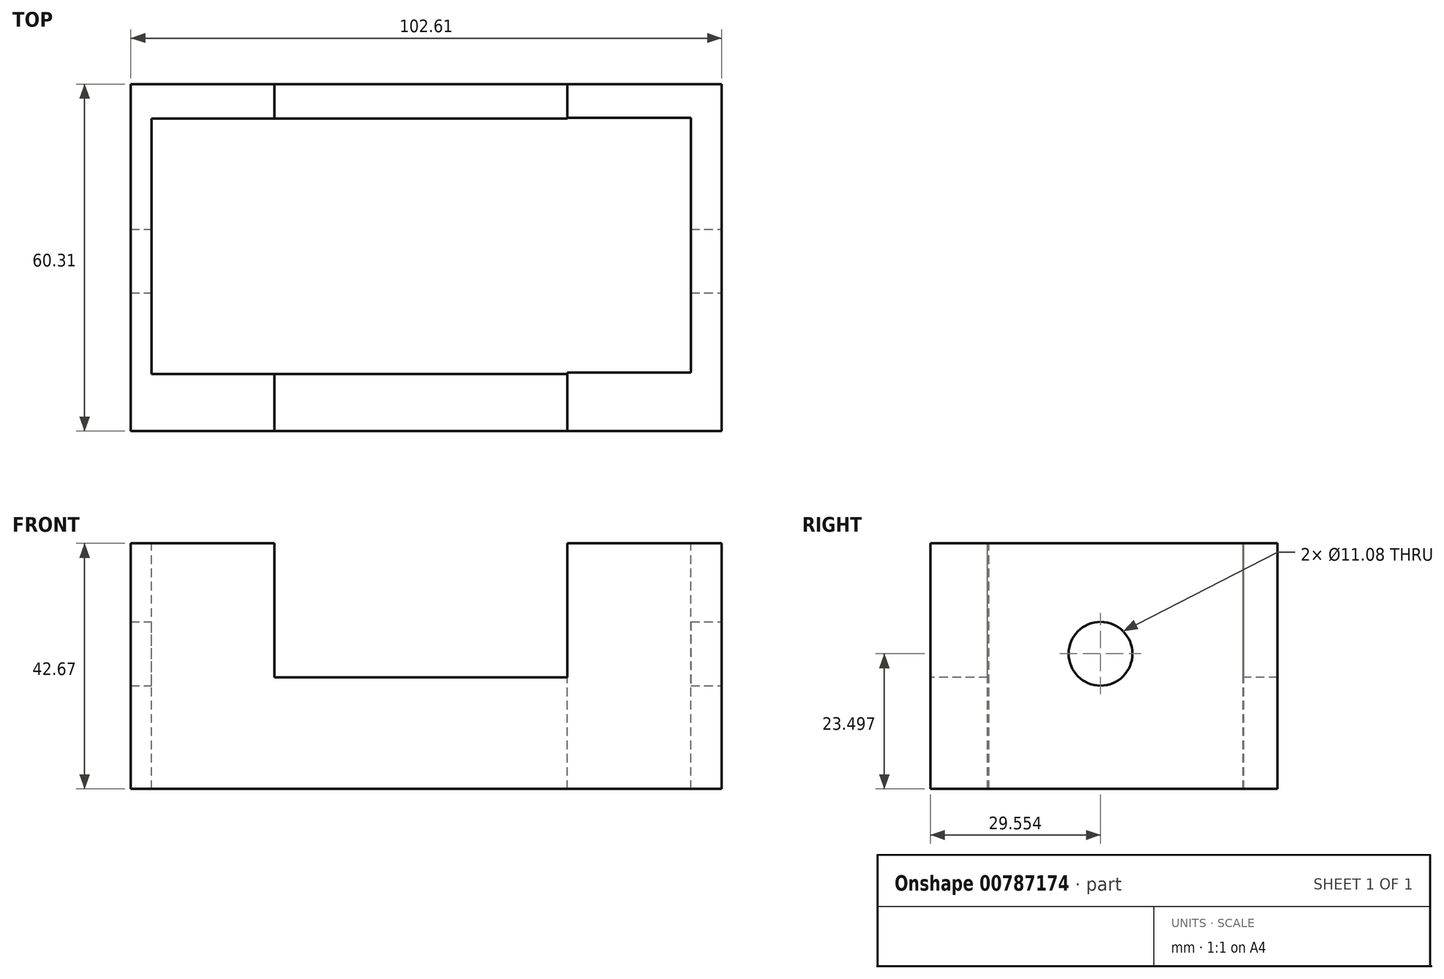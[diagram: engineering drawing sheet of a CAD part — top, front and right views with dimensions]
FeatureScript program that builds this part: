
annotation { "Feature Type Name" : "Feature", "Feature Type Description" : "" }
export const myFeature = defineFeature(function(context is Context, id is Id, definition is map)
    precondition{}
    {
        {
            var Q0;
            Q0=qCreatedBy(makeId("Top.planeOp"),FACE);
            var sketch = newSketch(context, id + "F0", { "sketchPlane" : qUnion([Q0])});
            skLineSegment(sketch, "E0.bottom", {"start": v(-54.23, 12.77) * mm, "end": v(48.38, 12.77) * mm});
            skLineSegment(sketch, "E0.top", {"start": v(-54.23, -47.54) * mm, "end": v(48.38, -47.54) * mm});
            skLineSegment(sketch, "E0.left", {"start": v(-54.23, 12.77) * mm, "end": v(-54.23, -47.54) * mm});
            skLineSegment(sketch, "E0.right", {"start": v(48.38, 12.77) * mm, "end": v(48.38, -47.54) * mm});
            skSolve(sketch);
        }
        {
            var Q0;
            Q0 = qSketchRegion(id + "F0", true);
            extrude(context, id + "F1", {"entities" : qUnion([Q0]), "depth" : 42.67 * mm, "offsetDistance" : 25.4 * mm});
        }
        {
            var Q0;
            Q0=makeQuery(id+"F1.opExtrude","SWEPT_FACE",FACE,{"disambiguationData":[OSD([sQuery(id+"F0.wireOp",EDGE,"E0.top")])]});
            var sketch = newSketch(context, id + "F2", { "sketchPlane" : qUnion([Q0])});
            skLineSegment(sketch, "E1", {"start": v(-29.28, 42.67) * mm, "end": v(-29.28, 19.4) * mm});
            skLineSegment(sketch, "E2", {"start": v(-29.28, 19.4) * mm, "end": v(21.57, 19.4) * mm});
            skLineSegment(sketch, "E3", {"start": v(21.57, 19.4) * mm, "end": v(21.57, 42.67) * mm});
            skLineSegment(sketch, "E4", {"start": v(21.57, 42.67) * mm, "end": v(-29.28, 42.67) * mm});
            skSolve(sketch);
        }
        {
            var Q0;
            Q0=makeQuery(id+"F2.imprint","IMPRINT",FACE,{"disambiguationData":[TD([[makeQuery(id+"F2.imprint","IMPRINT",EDGE,{"derivedFrom":sQuery(id+"F2.wireOp",EDGE,"E1")}),1.0]])]});
            extrude(context, id + "F3", {"entities" : qUnion([Q0]), "operationType" : NewBodyOperationType.REMOVE, "oppositeDirection" : true, "depth" : 108.7 * mm, "offsetDistance" : 25.4 * mm});
        }
        {
            var Q0;
            {var subQ0=sQuery(id+"F0.wireOp",EDGE,"E0.bottom");var subQ1=sQuery(id+"F0.wireOp",EDGE,"E0.top");var subQ2=sQuery(id+"F0.wireOp",EDGE,"E0.left");Q0=makeQuery(id+"F3.boolean.opBoolean","SPLIT",FACE,{"disambiguationData":[TD([makeQuery(id+"F1.opExtrude","SWEPT_FACE",FACE,{"disambiguationData":[OSD([subQ2])]})])],"derivedFrom":makeQuery(id+"F1.opExtrude","CAP_FACE",FACE,{"disambiguationData":[OSD([subQ0,subQ1,subQ2,sQuery(id+"F0.wireOp",EDGE,"E0.right")])],"isStart":false})});}
            var sketch = newSketch(context, id + "F4", { "sketchPlane" : qUnion([Q0])});
            skLineSegment(sketch, "E5", {"start": v(-54.23, -37.6) * mm, "end": v(-29.28, -37.6) * mm});
            skLineSegment(sketch, "E6", {"start": v(-50.59, -37.6) * mm, "end": v(-50.59, 6.75) * mm});
            skLineSegment(sketch, "E7", {"start": v(-29.28, 6.75) * mm, "end": v(-50.59, 6.75) * mm});
            skSolve(sketch);
        }
        {
            var Q0;
            {var subQ3=sQuery(id+"F4.wireOp",EDGE,"E6");Q0=makeQuery(id+"F4.imprint","IMPRINT",FACE,{"disambiguationData":[TD([[makeQuery(id+"F4.imprint","IMPRINT",EDGE,{"derivedFrom":subQ3}),-1.0]])]});}
            extrude(context, id + "F5", {"entities" : qUnion([Q0]), "operationType" : NewBodyOperationType.REMOVE, "oppositeDirection" : true, "depth" : 70.61 * mm, "offsetDistance" : 25.4 * mm});
        }
        {
            var Q0;
            Q0=makeQuery(id+"F3.boolean.opBoolean","COPY",FACE,{"derivedFrom":makeQuery(id+"F3.opExtrude","SWEPT_FACE",FACE,{"disambiguationData":[OSD([sQuery(id+"F2.wireOp",EDGE,"E2")])]})});
            var sketch = newSketch(context, id + "F6", { "sketchPlane" : qUnion([Q0])});
            skLineSegment(sketch, "E8", {"start": v(-29.28, -37.6) * mm, "end": v(21.57, -37.6) * mm});
            skLineSegment(sketch, "E9", {"start": v(-29.28, 6.75) * mm, "end": v(21.57, 6.75) * mm});
            skSolve(sketch);
        }
        {
            var Q0;
            {var subQ0=sQuery(id+"F6.wireOp",EDGE,"E8");Q0=makeQuery(id+"F6.imprint","IMPRINT",FACE,{"disambiguationData":[TD([[makeQuery(id+"F6.imprint","IMPRINT",EDGE,{"derivedFrom":subQ0}),1.0]])]});}
            extrude(context, id + "F7", {"entities" : qUnion([Q0]), "operationType" : NewBodyOperationType.REMOVE, "oppositeDirection" : true, "depth" : 37.6 * mm, "offsetDistance" : 25.4 * mm});
        }
        {
            var Q0;
            {var subQ0=sQuery(id+"F0.wireOp",EDGE,"E0.bottom");var subQ1=sQuery(id+"F0.wireOp",EDGE,"E0.right");var subQ2=sQuery(id+"F0.wireOp",EDGE,"E0.top");Q0=makeQuery(id+"F3.boolean.opBoolean","SPLIT",FACE,{"disambiguationData":[TD([makeQuery(id+"F1.opExtrude","SWEPT_FACE",FACE,{"disambiguationData":[OSD([subQ1])]})])],"derivedFrom":makeQuery(id+"F1.opExtrude","CAP_FACE",FACE,{"disambiguationData":[OSD([subQ0,subQ2,sQuery(id+"F0.wireOp",EDGE,"E0.left"),subQ1])],"isStart":false})});}
            var sketch = newSketch(context, id + "F8", { "sketchPlane" : qUnion([Q0])});
            skLineSegment(sketch, "E10", {"start": v(21.57, 6.92) * mm, "end": v(48.38, 6.92) * mm});
            skLineSegment(sketch, "E11", {"start": v(48.38, 6.92) * mm, "end": v(43.05, 6.92) * mm});
            skLineSegment(sketch, "E12", {"start": v(43.05, 6.92) * mm, "end": v(43.05, -37.39) * mm});
            skLineSegment(sketch, "E13", {"start": v(43.05, -37.39) * mm, "end": v(21.57, -37.39) * mm});
            skSolve(sketch);
        }
        {
            var Q0;
            {var subQ0=sQuery(id+"F8.wireOp",EDGE,"E10");Q0=makeQuery(id+"F8.imprint","IMPRINT",FACE,{"disambiguationData":[TD([[makeQuery(id+"F8.imprint","IMPRINT",EDGE,{"derivedFrom":subQ0}),-1.0]])]});}
            extrude(context, id + "F9", {"entities" : qUnion([Q0]), "operationType" : NewBodyOperationType.REMOVE, "oppositeDirection" : true, "depth" : 71.88 * mm, "offsetDistance" : 25.4 * mm});
        }
        {
            var Q0;
            Q0=makeQuery(id+"F1.opExtrude","SWEPT_FACE",FACE,{"disambiguationData":[OSD([sQuery(id+"F0.wireOp",EDGE,"E0.right")])]});
            var sketch = newSketch(context, id + "F10", { "sketchPlane" : qUnion([Q0])});
            skCircle(sketch, "E14", {"center": v(-17.99, 23.5) * mm, "radius": 5.54 * mm});
            skSolve(sketch);
        }
        {
            var Q0;
            Q0=makeQuery(id+"F10.imprint","IMPRINT",FACE,{"disambiguationData":[TD([[makeQuery(id+"F10.imprint","IMPRINT",EDGE,{"derivedFrom":sQuery(id+"F10.wireOp",EDGE,"E14")}),1.0]])]});
            extrude(context, id + "F11", {"entities" : qUnion([Q0]), "operationType" : NewBodyOperationType.REMOVE, "oppositeDirection" : true, "depth" : 182.63 * mm, "offsetDistance" : 25.4 * mm});
        }
    });
